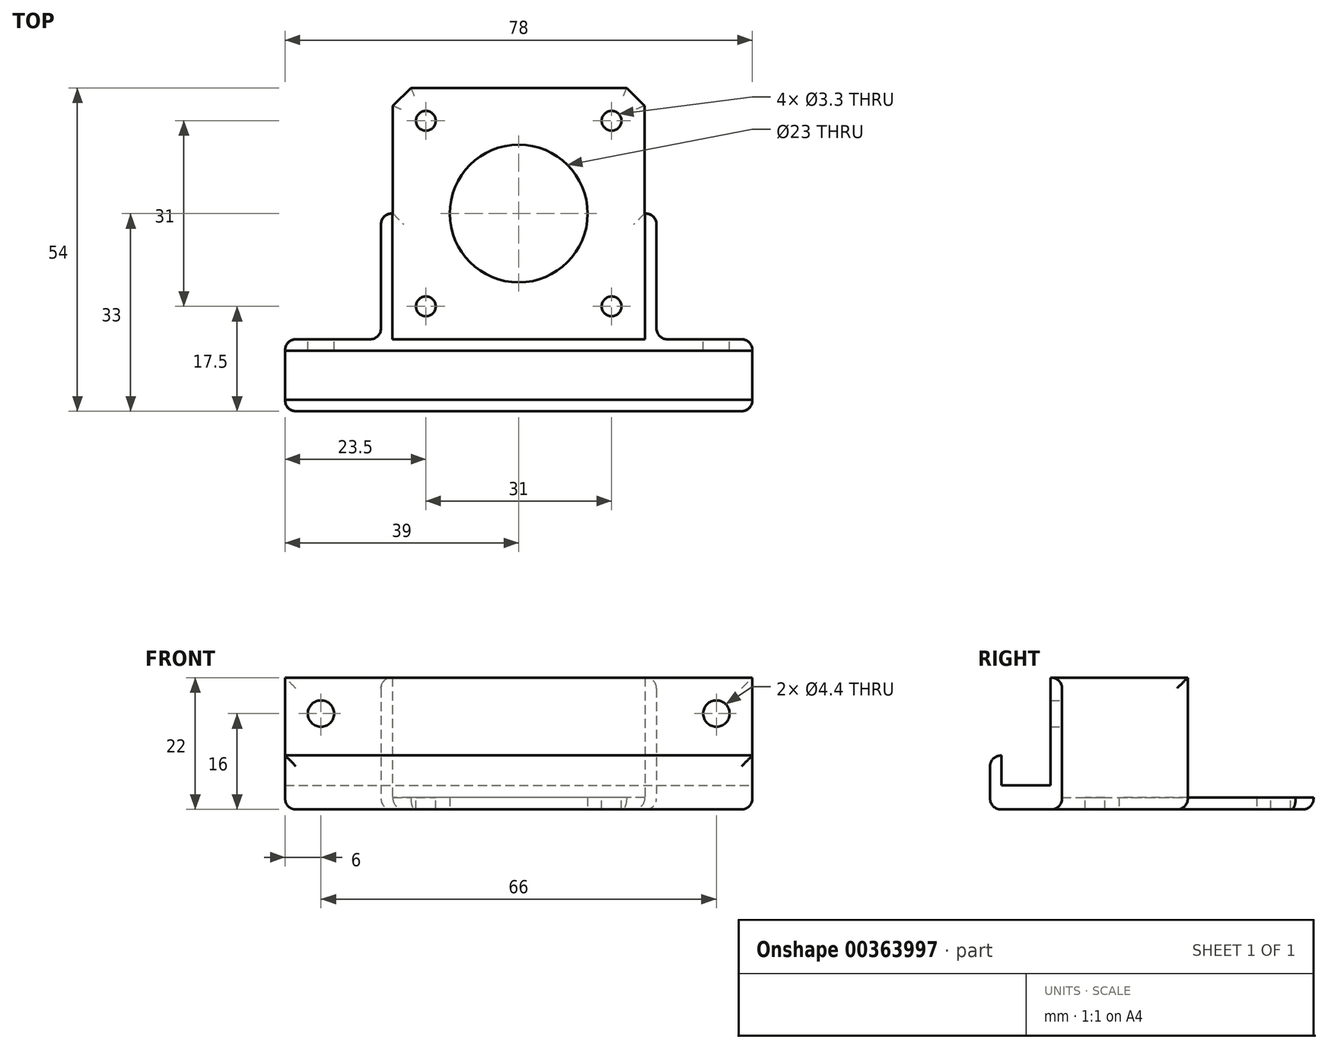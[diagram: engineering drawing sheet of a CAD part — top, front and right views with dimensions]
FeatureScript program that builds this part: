
annotation { "Feature Type Name" : "Feature", "Feature Type Description" : "" }
export const myFeature = defineFeature(function(context is Context, id is Id, definition is map)
    precondition{}
    {
        {
            var Q0;
            Q0=qCreatedBy(makeId("Top.planeOp"),FACE);
            var sketch = newSketch(context, id + "F0", { "sketchPlane" : qUnion([Q0])});
            skLineSegment(sketch, "E0", {"start": v(0, 0) * mm, "end": v(39, 0) * mm});
            skLineSegment(sketch, "E1", {"start": v(39, 0) * mm, "end": v(39, 12) * mm});
            skLineSegment(sketch, "E2", {"start": v(39, 12) * mm, "end": v(23, 12) * mm});
            skLineSegment(sketch, "E3", {"start": v(23, 12) * mm, "end": v(23, 33) * mm});
            skLineSegment(sketch, "E4", {"start": v(18, 54) * mm, "end": v(0, 54) * mm});
            skArc(sketch, "E5", {"start": v(0, 44.5) * mm, "mid": v(11.5, 33) * mm, "end": v(0, 21.5) * mm});
            skLineSegment(sketch, "E6", {"start": v(0, 54) * mm, "end": v(0, 44.5) * mm});
            skLineSegment(sketch, "E7", {"start": v(0, 0) * mm, "end": v(0, 21.5) * mm});
            skLineSegment(sketch, "E8", {"start": v(21, 51) * mm, "end": v(21, 33) * mm});
            skLineSegment(sketch, "E9", {"start": v(21, 33) * mm, "end": v(23, 33) * mm});
            skLineSegment(sketch, "E10", {"start": v(21, 51) * mm, "end": v(18, 54) * mm});
            skSolve(sketch);
        }
        {
            var Q0;
            Q0 = qSketchRegion(id + "F0", true);
            extrude(context, id + "F1", {"entities" : qUnion([Q0]), "depth" : 2 * mm, "offsetDistance" : 25 * mm});
        }
        {
            var Q0;
            Q0=makeQuery(id+"F1.opExtrude","CAP_FACE",FACE,{"disambiguationData":[OSD([sQuery(id+"F0.wireOp",EDGE,"E0"),sQuery(id+"F0.wireOp",EDGE,"E1"),sQuery(id+"F0.wireOp",EDGE,"E2"),sQuery(id+"F0.wireOp",EDGE,"E3"),sQuery(id+"F0.wireOp",EDGE,"E4"),sQuery(id+"F0.wireOp",EDGE,"GTK3j6eS-NkKF-EAMN-Qrw0-I8KsfHH8vVhG")])],"isStart":false});
            var sketch = newSketch(context, id + "F2", { "sketchPlane" : qUnion([Q0])});
            skLineSegment(sketch, "E11", {"start": v(0, 0) * mm, "end": v(39, 0) * mm});
            skLineSegment(sketch, "E12", {"start": v(39, 12) * mm, "end": v(39, 0) * mm});
            skLineSegment(sketch, "E13", {"start": v(39, 12) * mm, "end": v(23, 12) * mm});
            skLineSegment(sketch, "E14", {"start": v(21.1, 12) * mm, "end": v(0, 12) * mm});
            skLineSegment(sketch, "E15", {"start": v(0, 0) * mm, "end": v(0, 12) * mm});
            skLineSegment(sketch, "E16", {"start": v(21.1, 12) * mm, "end": v(21.1, 33) * mm});
            skLineSegment(sketch, "E17", {"start": v(21.1, 33) * mm, "end": v(23, 33) * mm});
            skLineSegment(sketch, "E18", {"start": v(23, 33) * mm, "end": v(23, 12) * mm});
            skSolve(sketch);
        }
        {
            var Q0;
            Q0 = qSketchRegion(id + "F2", true);
            extrude(context, id + "F3", {"entities" : qUnion([Q0]), "operationType" : NewBodyOperationType.ADD, "depth" : 2 * mm, "offsetDistance" : 25 * mm});
        }
        {
            var Q0;
            Q0=makeQuery(id+"F3.opExtrude","CAP_FACE",FACE,{"disambiguationData":[OSD([sQuery(id+"F2.wireOp",EDGE,"E11"),sQuery(id+"F2.wireOp",EDGE,"E12"),sQuery(id+"F2.wireOp",EDGE,"E13"),sQuery(id+"F2.wireOp",EDGE,"E14"),sQuery(id+"F2.wireOp",EDGE,"E15"),sQuery(id+"F2.wireOp",EDGE,"E16"),sQuery(id+"F2.wireOp",EDGE,"E17"),sQuery(id+"F2.wireOp",EDGE,"E18")])],"isStart":false});
            var sketch = newSketch(context, id + "F4", { "sketchPlane" : qUnion([Q0])});
            skLineSegment(sketch, "E19", {"start": v(21.1, 33) * mm, "end": v(21.1, 12) * mm});
            skLineSegment(sketch, "E20", {"start": v(21.1, 12) * mm, "end": v(0, 12) * mm});
            skLineSegment(sketch, "E21", {"start": v(0, 12) * mm, "end": v(0, 10.1) * mm});
            skLineSegment(sketch, "E22", {"start": v(0, 10.1) * mm, "end": v(39, 10.1) * mm});
            skLineSegment(sketch, "E23", {"start": v(39, 10.1) * mm, "end": v(39, 12) * mm});
            skLineSegment(sketch, "E24", {"start": v(39, 12) * mm, "end": v(23, 12) * mm});
            skLineSegment(sketch, "E25", {"start": v(23, 12) * mm, "end": v(23, 33) * mm});
            skLineSegment(sketch, "E26", {"start": v(23, 33) * mm, "end": v(21.1, 33) * mm});
            skSolve(sketch);
        }
        {
            var Q0;
            Q0 = qSketchRegion(id + "F4", true);
            extrude(context, id + "F5", {"entities" : qUnion([Q0]), "operationType" : NewBodyOperationType.ADD, "depth" : 18 * mm, "offsetDistance" : 25 * mm});
        }
        {
            var Q0;
            Q0=makeQuery(id+"F3.opExtrude","CAP_FACE",FACE,{"disambiguationData":[OSD([sQuery(id+"F2.wireOp",EDGE,"E11"),sQuery(id+"F2.wireOp",EDGE,"E12"),sQuery(id+"F2.wireOp",EDGE,"E13"),sQuery(id+"F2.wireOp",EDGE,"E14"),sQuery(id+"F2.wireOp",EDGE,"E15"),sQuery(id+"F2.wireOp",EDGE,"E16"),sQuery(id+"F2.wireOp",EDGE,"E17"),sQuery(id+"F2.wireOp",EDGE,"E18")])],"isStart":false});
            var sketch = newSketch(context, id + "F6", { "sketchPlane" : qUnion([Q0])});
            skLineSegment(sketch, "E27.bottom", {"start": v(0, 0) * mm, "end": v(39, 0) * mm});
            skLineSegment(sketch, "E27.top", {"start": v(0, 1.9) * mm, "end": v(39, 1.9) * mm});
            skLineSegment(sketch, "E27.left", {"start": v(0, 0) * mm, "end": v(0, 1.9) * mm});
            skLineSegment(sketch, "E27.right", {"start": v(39, 0) * mm, "end": v(39, 1.9) * mm});
            skSolve(sketch);
        }
        {
            var Q0;
            Q0 = qSketchRegion(id + "F6", true);
            extrude(context, id + "F7", {"entities" : qUnion([Q0]), "operationType" : NewBodyOperationType.ADD, "depth" : 5 * mm, "offsetDistance" : 25 * mm});
        }
        {
            var Q0;
            Q0=makeQuery(id+"F1.opExtrude","CAP_FACE",FACE,{"disambiguationData":[OSD([sQuery(id+"F0.wireOp",EDGE,"E0"),sQuery(id+"F0.wireOp",EDGE,"E1"),sQuery(id+"F0.wireOp",EDGE,"E2"),sQuery(id+"F0.wireOp",EDGE,"E3"),sQuery(id+"F0.wireOp",EDGE,"E4"),sQuery(id+"F0.wireOp",EDGE,"E5"),sQuery(id+"F0.wireOp",EDGE,"E6"),sQuery(id+"F0.wireOp",EDGE,"E7")])],"isStart":true});
            var sketch = newSketch(context, id + "F8", { "sketchPlane" : qUnion([Q0])});
            skPoint(sketch, "E28", {"position": v(15.5, -17.5) * mm});
            skPoint(sketch, "E29", {"position": v(15.5, -48.5) * mm});
            skSolve(sketch);
        }
        {
            var Q0;
            Q0=sQuery(id+"F8.wireOp",VERTEX,"E28");
            var Q1;
            Q1=sQuery(id+"F8.wireOp",VERTEX,"E29");
            var Q2;
            Q2=makeQuery(id+"F1.opExtrude","SWEPT_BODY",BODY,{"disambiguationData":[OSD([sQuery(id+"F0.wireOp",EDGE,"E0"),sQuery(id+"F0.wireOp",EDGE,"E1"),sQuery(id+"F0.wireOp",EDGE,"E2"),sQuery(id+"F0.wireOp",EDGE,"E3"),sQuery(id+"F0.wireOp",EDGE,"E4"),sQuery(id+"F0.wireOp",EDGE,"E5"),sQuery(id+"F0.wireOp",EDGE,"E6"),sQuery(id+"F0.wireOp",EDGE,"E7")])]});
            hole(context, id + "F9", {"style" : HoleStyle.SIMPLE, "endStyle" : HoleEndStyle.BLIND, "standardTappedOrClearance" : lookupTablePath({ "standard" : "ISO", "fit" : "Normal", "size" : "M3", "type" : "Clearance" }), "standardBlindInLast" : lookupTablePath({ "fit" : "Standard", "standard" : "ISO", "size" : "M3", "type" : "Clearance" }), "holeDiameter" : 3.3 * mm, "majorDiameter" : 5 * mm, "holeDepth" : 8 * mm, "isTappedThrough" : true, "tappedDepth" : 12 * mm, "tapClearance" : 3, "locations" : qUnion([Q0, Q1]), "scope" : qUnion([Q2]), "startStyle" : HoleStartStyle.PART});
        }
        {
            var Q0;
            Q0=makeQuery(id+"F5.opExtrude","SWEPT_FACE",FACE,{"disambiguationData":[OSD([sQuery(id+"F4.wireOp",EDGE,"E22")])]});
            var sketch = newSketch(context, id + "F10", { "sketchPlane" : qUnion([Q0])});
            skPoint(sketch, "E30", {"position": v(33, 16) * mm});
            skSolve(sketch);
        }
        {
            var Q0;
            Q0=sQuery(id+"F10.wireOp",VERTEX,"E30");
            var Q1;
            Q1=makeQuery(id+"F1.opExtrude","SWEPT_BODY",BODY,{"disambiguationData":[OSD([sQuery(id+"F0.wireOp",EDGE,"E0"),sQuery(id+"F0.wireOp",EDGE,"E1"),sQuery(id+"F0.wireOp",EDGE,"E2"),sQuery(id+"F0.wireOp",EDGE,"E3"),sQuery(id+"F0.wireOp",EDGE,"E4"),sQuery(id+"F0.wireOp",EDGE,"E5"),sQuery(id+"F0.wireOp",EDGE,"E6"),sQuery(id+"F0.wireOp",EDGE,"E7")])]});
            hole(context, id + "F11", {"style" : HoleStyle.SIMPLE, "endStyle" : HoleEndStyle.BLIND, "standardTappedOrClearance" : lookupTablePath({ "standard" : "ISO", "fit" : "Normal", "size" : "M4", "type" : "Clearance" }), "standardBlindInLast" : lookupTablePath({ "fit" : "Standard", "standard" : "ISO", "size" : "M4", "type" : "Clearance" }), "holeDiameter" : 4.4 * mm, "majorDiameter" : 5 * mm, "holeDepth" : 8 * mm, "isTappedThrough" : true, "tappedDepth" : 12 * mm, "tapClearance" : 3, "locations" : qUnion([Q0]), "scope" : qUnion([Q1]), "startStyle" : HoleStartStyle.PART});
        }
        {
            var Q0;
            Q0=makeQuery(id+"F5.opExtrude","CAP_EDGE",EDGE,{"disambiguationData":[OSD([sQuery(id+"F4.wireOp",EDGE,"E24")])],"isStart":false});
            var Q1;
            Q1=makeQuery(id+"F5.boolean.opBoolean","MERGE",EDGE,{"derivedFrom":[makeQuery(id+"F3.boolean.opBoolean","MERGE",EDGE,{"derivedFrom":[makeQuery(id+"F1.opExtrude","SWEPT_EDGE",EDGE,{"disambiguationData":[OSD([sQuery(id+"F0.wireOp",EDGE,"E1"),sQuery(id+"F0.wireOp",EDGE,"E2")])]}),makeQuery(id+"F3.opExtrude","SWEPT_EDGE",EDGE,{"disambiguationData":[OSD([sQuery(id+"F2.wireOp",EDGE,"E12"),sQuery(id+"F2.wireOp",EDGE,"E13")])]})]}),makeQuery(id+"F5.opExtrude","SWEPT_EDGE",EDGE,{"disambiguationData":[OSD([sQuery(id+"F4.wireOp",EDGE,"E23"),sQuery(id+"F4.wireOp",EDGE,"E24")])]})]});
            var Q2;
            Q2=makeQuery(id+"F5.boolean.opBoolean","MERGE",EDGE,{"derivedFrom":[makeQuery(id+"F3.opExtrude","SWEPT_EDGE",EDGE,{"disambiguationData":[OSD([sQuery(id+"F0.wireOp",EDGE,"E3"),sQuery(id+"F2.wireOp",EDGE,"E17"),sQuery(id+"F2.wireOp",EDGE,"E18")])]}),makeQuery(id+"F5.opExtrude","SWEPT_EDGE",EDGE,{"disambiguationData":[OSD([sQuery(id+"F4.wireOp",EDGE,"E25"),sQuery(id+"F4.wireOp",EDGE,"E26")])]})]});
            var Q3;
            Q3=makeQuery(id+"F5.opExtrude","CAP_EDGE",EDGE,{"disambiguationData":[OSD([sQuery(id+"F4.wireOp",EDGE,"E25")])],"isStart":false});
            var Q4;
            Q4=makeQuery(id+"F1.opExtrude","CAP_EDGE",EDGE,{"disambiguationData":[OSD([sQuery(id+"F0.wireOp",EDGE,"E3")])],"isStart":true});
            var Q5;
            Q5=makeQuery(id+"F1.opExtrude","CAP_EDGE",EDGE,{"disambiguationData":[OSD([sQuery(id+"F0.wireOp",EDGE,"E4")])],"isStart":true});
            var Q6;
            Q6=makeQuery(id+"F1.opExtrude","CAP_EDGE",EDGE,{"disambiguationData":[OSD([sQuery(id+"F0.wireOp",EDGE,"E2")])],"isStart":true});
            var Q7;
            Q7=makeQuery(id+"F5.boolean.opBoolean","MERGE",EDGE,{"derivedFrom":[makeQuery(id+"F3.boolean.opBoolean","MERGE",EDGE,{"derivedFrom":[makeQuery(id+"F1.opExtrude","SWEPT_EDGE",EDGE,{"disambiguationData":[OSD([sQuery(id+"F0.wireOp",EDGE,"E2"),sQuery(id+"F0.wireOp",EDGE,"E3")])]}),makeQuery(id+"F3.opExtrude","SWEPT_EDGE",EDGE,{"disambiguationData":[OSD([sQuery(id+"F2.wireOp",EDGE,"E13"),sQuery(id+"F2.wireOp",EDGE,"E18")])]})]}),makeQuery(id+"F5.opExtrude","SWEPT_EDGE",EDGE,{"disambiguationData":[OSD([sQuery(id+"F4.wireOp",EDGE,"E24"),sQuery(id+"F4.wireOp",EDGE,"E25")])]})]});
            var Q8;
            Q8=makeQuery(id+"F1.opExtrude","CAP_EDGE",EDGE,{"disambiguationData":[OSD([sQuery(id+"F0.wireOp",EDGE,"E1")])],"isStart":true});
            var Q9;
            Q9=makeQuery(id+"F7.opExtrude","CAP_EDGE",EDGE,{"disambiguationData":[OSD([sQuery(id+"F6.wireOp",EDGE,"E27.bottom")])],"isStart":false});
            var Q10;
            Q10=makeQuery(id+"F1.opExtrude","CAP_EDGE",EDGE,{"disambiguationData":[OSD([sQuery(id+"F0.wireOp",EDGE,"E0")])],"isStart":true});
            var Q11;
            Q11=makeQuery(id+"F7.boolean.opBoolean","MERGE",EDGE,{"derivedFrom":[makeQuery(id+"F3.boolean.opBoolean","MERGE",EDGE,{"derivedFrom":[makeQuery(id+"F1.opExtrude","SWEPT_EDGE",EDGE,{"disambiguationData":[OSD([sQuery(id+"F0.wireOp",EDGE,"E0"),sQuery(id+"F0.wireOp",EDGE,"E1")])]}),makeQuery(id+"F3.opExtrude","SWEPT_EDGE",EDGE,{"disambiguationData":[OSD([sQuery(id+"F2.wireOp",EDGE,"E11"),sQuery(id+"F2.wireOp",EDGE,"E12")])]})]}),makeQuery(id+"F7.opExtrude","SWEPT_EDGE",EDGE,{"disambiguationData":[OSD([sQuery(id+"F6.wireOp",EDGE,"E27.bottom"),sQuery(id+"F6.wireOp",EDGE,"E27.right")])]})]});
            var Q12;
            Q12=makeQuery(id+"F1.opExtrude","CAP_EDGE",EDGE,{"disambiguationData":[OSD([sQuery(id+"F0.wireOp",EDGE,"E8")])],"isStart":true});
            var Q13;
            Q13=makeQuery(id+"F1.opExtrude","CAP_EDGE",EDGE,{"disambiguationData":[OSD([sQuery(id+"F0.wireOp",EDGE,"E9")])],"isStart":true});
            var Q14;
            Q14=makeQuery(id+"F1.opExtrude","CAP_EDGE",EDGE,{"disambiguationData":[OSD([sQuery(id+"F0.wireOp",EDGE,"E10")])],"isStart":true});
            fillet(context, id + "F12", {"entities" : qUnion([Q0, Q1, Q2, Q3, Q4, Q5, Q6, Q7, Q8, Q9, Q10, Q11, Q12, Q13, Q14]), "radius" : 1.8 * mm, "tangentPropagation" : true, "allowEdgeOverflow" : false});
        }
        {
            var Q0;
            Q0=makeQuery(id+"F1.opExtrude","SWEPT_BODY",BODY,{"disambiguationData":[OSD([sQuery(id+"F0.wireOp",EDGE,"E0"),sQuery(id+"F0.wireOp",EDGE,"E1"),sQuery(id+"F0.wireOp",EDGE,"E2"),sQuery(id+"F0.wireOp",EDGE,"E3"),sQuery(id+"F0.wireOp",EDGE,"E4"),sQuery(id+"F0.wireOp",EDGE,"E5"),sQuery(id+"F0.wireOp",EDGE,"E6"),sQuery(id+"F0.wireOp",EDGE,"E7")])]});
            var Q1;
            Q1=qCreatedBy(makeId("Right.planeOp"),FACE);
            mirror(context, id + "F13", {"operationType" : NewBodyOperationType.ADD, "entities" : qUnion([Q0]), "mirrorPlane" : qUnion([Q1])});
        }
    });
